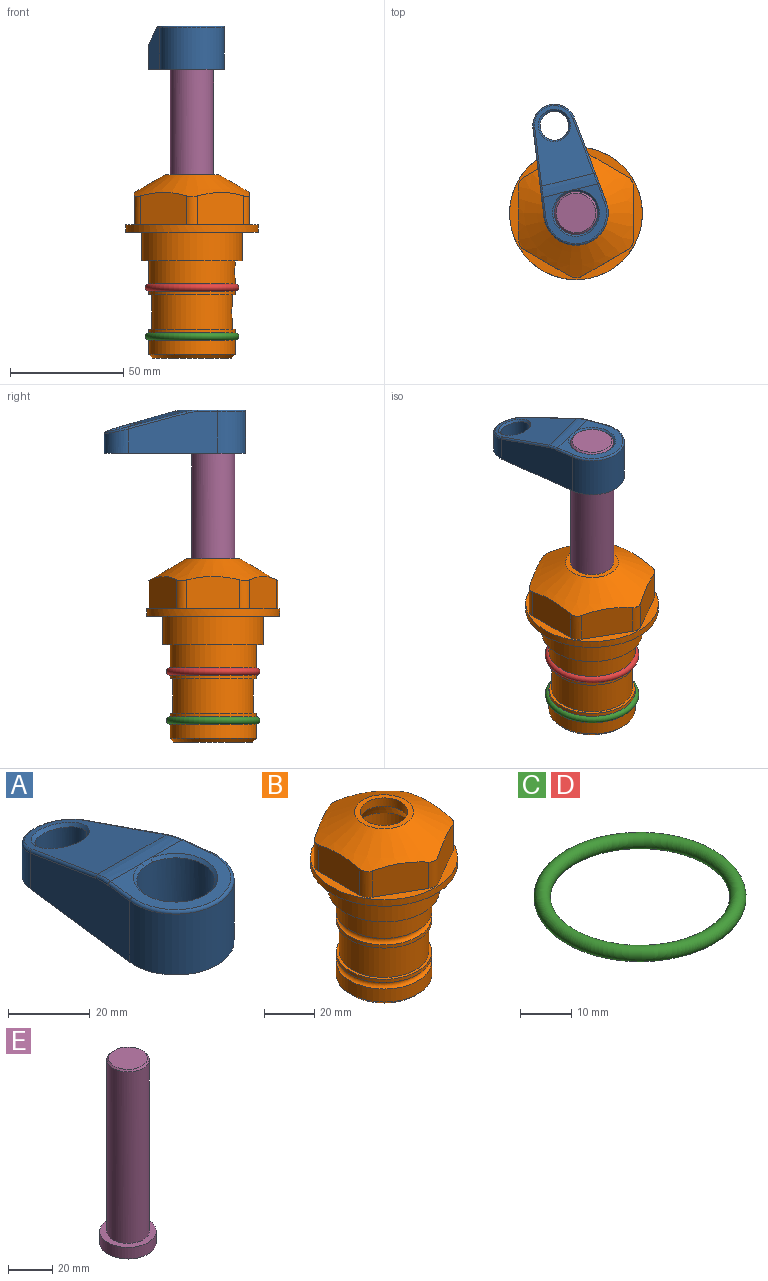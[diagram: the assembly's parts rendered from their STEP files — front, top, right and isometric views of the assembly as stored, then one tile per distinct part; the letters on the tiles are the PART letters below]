
ASSEMBLY  parts=5 mates=4
PART A: 31 faces, bbox 31.7x65.5x19.8 mm
  f0: plane 39.12x18.26mm, normal (0.99,0.12,0), area 612.2mm2, adj f1,f4,f7,f11,f13,f15
  f1: cylinder r=9.53mm len=18.91mm, axis (0,0,-1), area 296.1mm2, adj f0,f2,f7,f17
  f2: plane 39.12x18.26mm, normal (-0.99,0.12,0), area 612.2mm2, adj f1,f4,f7,f12,f14,f16
  f3: cylinder r=6.35mm len=12.7mm, axis (0,0,-1), area 362.4mm2, adj f7,f18
  f4: cylinder r=14.29mm len=28.58mm, axis (0,0,-1), area 882.2mm2, adj f0,f2,f7,f10
  f5: cylinder r=9.53mm len=19.05mm, axis (0,0,-1), area 1092.6mm2, adj f7,f19,f20
  f6: plane 26.99x23.69mm, normal (0,0,1), area 216.2mm2, adj f9,f10,f11,f12,f19
  f7: plane 63.5x28.58mm, normal (0,0,-1), area 661.8mm2, adj f0,f1,f2,f3,f4,f5,f22,f23
  f8: plane 33.52x23.6mm, normal (0,0.26,0.97), area 486mm2, adj f9,f15,f16,f17,f18
  f9: cylinder r=19.05mm len=24.72mm, axis (1,0,0), area 120.4mm2, adj f6,f8,f13,f14,f20
  f10: torus R=13.49mm, axis (0,0,1), area 59mm2, adj f4,f6,f11,f12
  f11: cylinder r=0.79mm len=8.67mm, axis (0.12,-0.99,0), area 10.8mm2, adj f0,f6,f10,f13
  f12: cylinder r=0.79mm len=8.67mm, axis (0.12,0.99,0), area 10.8mm2, adj f2,f6,f10,f14
  f13: bspline ~4.95x1.42mm, area 6.1mm2, adj f0,f9,f11,f15
  f14: bspline ~4.95x1.42mm, area 6.1mm2, adj f2,f9,f12,f16
  f15: cylinder r=0.79mm len=25.95mm, axis (0.12,-0.96,0.26), area 32.9mm2, adj f0,f8,f13,f17
  f16: cylinder r=0.79mm len=25.95mm, axis (0.12,0.96,-0.26), area 32.9mm2, adj f2,f8,f14,f17
  f17: bspline ~18.91x8.38mm, area 30mm2, adj f1,f8,f15,f16
  f18: bspline ~14.29x14.29mm, area 48.3mm2, adj f3,f8
  f19: cone r=9.53mm half-angle=45deg, axis (0,0,1), area 66.5mm2, adj f5,f6,f20
  f20: bspline ~3.22x0.96mm, area 3.5mm2, adj f5,f9,f19
  f21: plane 2.75x2.72mm, normal (0,0,-1), area 2.9mm2, adj f23,f25,f28
  f22: plane 23.05x15.88mm, normal (-0.99,-0.12,0), area 323.6mm2, adj f7,f25,f26,f27,f28,f29
  f23: plane 23.05x15.88mm, normal (0.99,-0.12,0), area 323.6mm2, adj f7,f21,f25,f27,f28,f30
  f24: cylinder r=9.53mm len=10.69mm, axis (0,0,-1), area 114.7mm2, adj f7,f27,f29,f30
  f25: cylinder r=12.7mm len=20.59mm, axis (0,0,-1), area 381.1mm2, adj f7,f21,f22,f23,f26,f28
  f26: plane 2.75x2.72mm, normal (0,0,-1), area 2.9mm2, adj f22,f25,f28
  f27: plane 19.72x18.37mm, normal (0,-0.26,-0.97), area 291.8mm2, adj f22,f23,f24,f28,f29,f30
  f28: cylinder r=15.88mm len=19.92mm, axis (1,0,0), area 54.8mm2, adj f21,f22,f23,f25,f26,f27
  f29: cylinder r=1.59mm len=11mm, axis (0,0,-1), area 34.7mm2, adj f7,f22,f24,f27
  f30: cylinder r=1.59mm len=11mm, axis (0,0,-1), area 34.7mm2, adj f7,f23,f24,f27
PART B: 36 faces, bbox 58.7x58.7x81 mm
  f0: cylinder r=17.78mm len=35.56mm, axis (0,0,1), area 1670.8mm2, adj f23,f24,f31
  f1: cylinder r=19.05mm len=38.1mm, axis (0,0,1), area 1191.9mm2, adj f26,f27,f30
  f2: plane 58.66x58.66mm, normal (0,0,-1), area 1150.6mm2, adj f3,f28
  f3: cylinder r=29.33mm len=58.66mm, axis (0,0,-1), area 585.1mm2, adj f2,f4
  f4: plane 58.66x58.66mm, normal (0,0,1), area 475.9mm2, adj f3,f5,f6,f7,f8,f9,f10,f11
  f5: plane 20.32x14.34mm, normal (-0.5,0.87,0), area 324.4mm2, adj f4,f15,f16,f17
  f6: plane 20.32x14.34mm, normal (0.5,0.87,0), area 324.4mm2, adj f4,f14,f15,f17
  f7: plane 23.48x14.34mm, normal (1,0,0), area 324.4mm2, adj f4,f13,f14,f17
  f8: plane 20.32x14.34mm, normal (0.5,-0.87,0), area 324.4mm2, adj f4,f12,f13,f17
  f9: plane 20.32x14.34mm, normal (-0.5,-0.87,0), area 324.4mm2, adj f4,f11,f12,f17
  f10: plane 23.48x14.34mm, normal (-1,0,0), area 324.4mm2, adj f4,f11,f16,f17
  f11: cylinder r=5.08mm len=12.85mm, axis (0,0,-1), area 67.2mm2, adj f4,f9,f10,f17
  f12: cylinder r=5.08mm len=12.85mm, axis (0,0,-1), area 67.2mm2, adj f4,f8,f9,f17
  f13: cylinder r=5.08mm len=12.85mm, axis (0,0,-1), area 67.2mm2, adj f4,f7,f8,f17
  f14: cylinder r=5.08mm len=12.85mm, axis (0,0,-1), area 67.2mm2, adj f4,f6,f7,f17
  f15: cylinder r=5.08mm len=12.85mm, axis (0,0,-1), area 67.2mm2, adj f4,f5,f6,f17
  f16: cylinder r=5.08mm len=12.85mm, axis (0,0,-1), area 67.2mm2, adj f4,f5,f10,f17
  f17: cone r=11.73mm half-angle=60deg, axis (0,0,-1), area 2071.8mm2, adj f5,f6,f7,f8,f9,f10,f11,f12
  f18: plane 23.46x23.46mm, normal (0,0,1), area 147.4mm2, adj f17,f35
  f19: plane 34.93x34.93mm, normal (0,0,-1), area 958mm2, adj f29
  f20: cylinder r=19.05mm len=38.1mm, axis (0,0,1), area 760.1mm2, adj f21,f29
  f21: torus R=19.05mm, axis (0,0,1), area 565.3mm2, adj f20,f22
  f22: cylinder r=19.05mm len=38.1mm, axis (0,0,1), area 190mm2, adj f21,f23
  f23: plane 38.1x38.1mm, normal (0,0,1), area 146.9mm2, adj f0,f22
  f24: plane 38.1x38.1mm, normal (0,0,-1), area 146.9mm2, adj f0,f25
  f25: cylinder r=19.05mm len=38.1mm, axis (0,0,1), area 190mm2, adj f24,f26
  f26: torus R=19.05mm, axis (0,0,1), area 565.3mm2, adj f1,f25
  f27: plane 44.45x44.45mm, normal (0,0,-1), area 411.7mm2, adj f1,f28
  f28: cylinder r=22.23mm len=44.45mm, axis (0,0,1), area 1773.5mm2, adj f2,f27
  f29: cone r=19.05mm half-angle=45deg, axis (0,0,1), area 257.5mm2, adj f19,f20
  f30: cylinder r=3.17mm len=6.75mm, axis (-1,0,0), area 128mm2, adj f1,f33
  f31: cylinder r=3.17mm len=6.35mm, axis (-1,0,0), area 102.5mm2, adj f0,f33
  f32: plane 25.4x25.4mm, normal (0,0,1), area 506.7mm2, adj f33
  f33: cylinder r=12.7mm len=66.42mm, axis (0,0,-1), area 5236.2mm2, adj f30,f31,f32,f34
  f34: cone r=9.53mm half-angle=30deg, axis (0,0,-1), area 443.4mm2, adj f33,f35
  f35: cylinder r=9.53mm len=19.05mm, axis (0,0,-1), area 240.9mm2, adj f18,f34
PART C: 1 faces, bbox 44.7x44.7x3.2 mm
  f0: torus R=19.05mm, axis (0,0,1), area 1193.9mm2
PART D: same geometry as C
PART E: 6 faces, bbox 25.4x25.4x101.6 mm
  f0: plane 17.46x17.46mm, normal (0,0,1), area 239.5mm2, adj f5
  f1: plane 25.4x25.4mm, normal (0,0,-1), area 506.7mm2, adj f2
  f2: cylinder r=12.7mm len=25.4mm, axis (0,0,1), area 506.7mm2, adj f1,f3
  f3: plane 25.4x25.4mm, normal (0,0,1), area 221.7mm2, adj f2,f4
  f4: cylinder r=9.53mm len=94.46mm, axis (0,0,1), area 5653mm2, adj f3,f5
  f5: cone r=8.73mm half-angle=45deg, axis (0,0,-1), area 64.4mm2, adj f0,f4
PLACE A rot(axis=(0,0,1),13.9deg) t=(0,0,27.55)mm
PLACE B at identity fixed
PLACE C t=(0,0,-21.59)mm
PLACE D at identity
PLACE E rot(axis=(0,0,1),13.9deg) t=(0,0,27.55)mm
MATE fastened C.f0 <-> B.f0  axis (0,0,1) through (0,0,-46.1)mm
MATE fastened D.f0 <-> B.f0  axis (0,0,1) through (0,0,-24.51)mm
MATE fastened A.f4 <-> E.f2  axis (0,0,1) through (0,0,91.05)mm
MATE cylindrical E.f2 <-> B.f0  axis (0,0,-1) through (0,0,-10.55)mm
